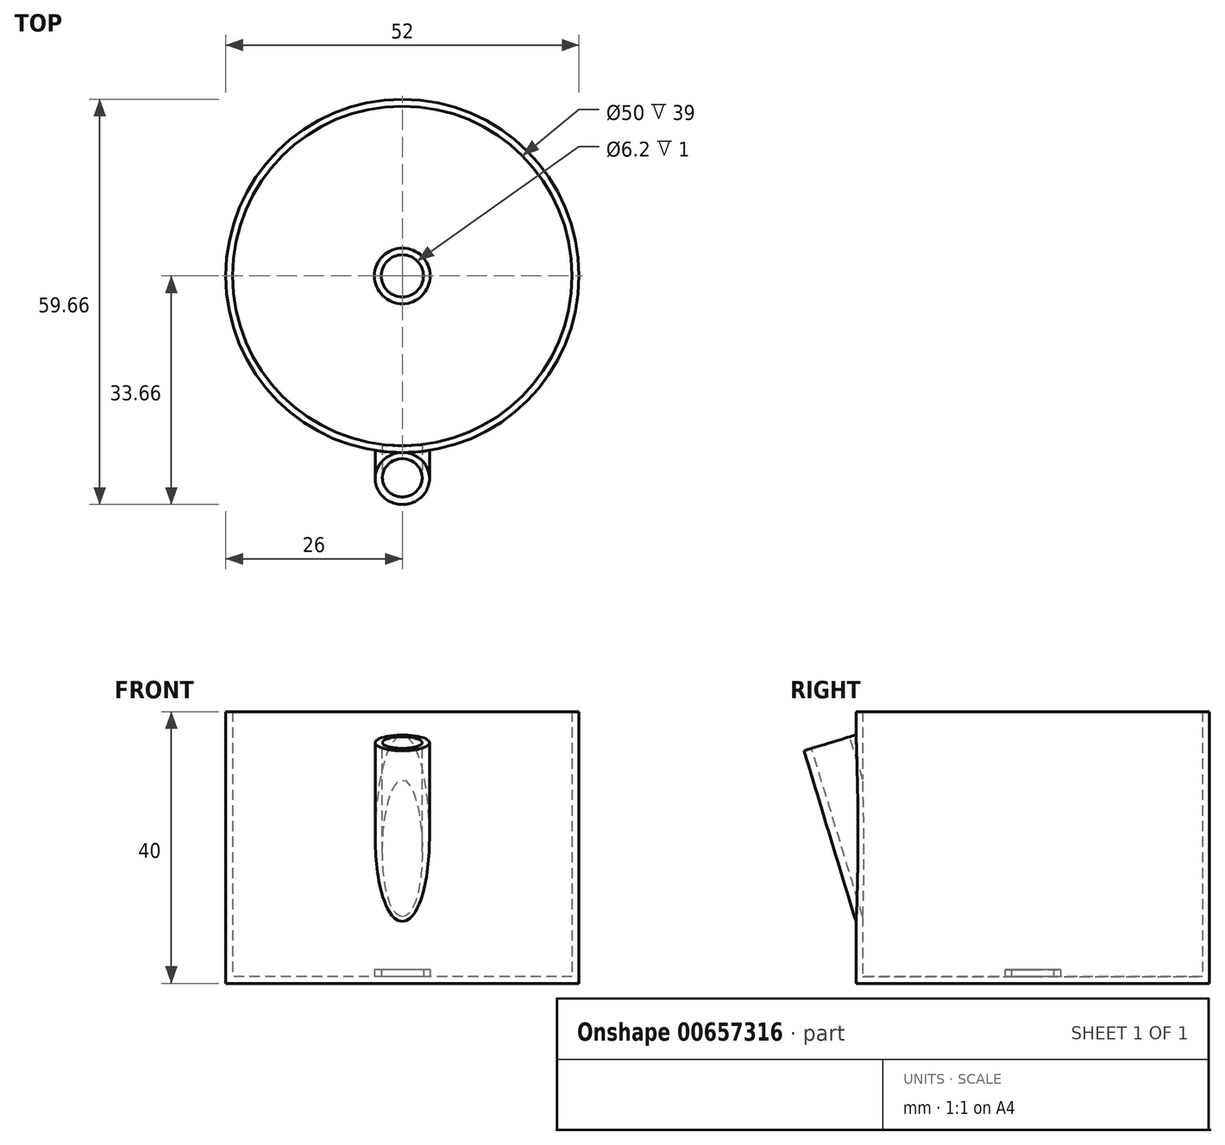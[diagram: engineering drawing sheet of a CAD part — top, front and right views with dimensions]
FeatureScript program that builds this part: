
annotation { "Feature Type Name" : "Feature", "Feature Type Description" : "" }
export const myFeature = defineFeature(function(context is Context, id is Id, definition is map)
    precondition{}
    {
        {
            var Q0;
            Q0=qCreatedBy(makeId("Top.planeOp"),FACE);
            var sketch = newSketch(context, id + "F0", { "sketchPlane" : qUnion([Q0])});
            skCircle(sketch, "E0", {"center": v(0, 0) * mm, "radius": 25 * mm});
            skCircle(sketch, "E1", {"center": v(0, 0) * mm, "radius": 26 * mm});
            skSolve(sketch);
        }
        {
            var Q0;
            Q0=makeQuery(id+"F0.imprint","IMPRINT",FACE,{"disambiguationData":[TD([[makeQuery(id+"F0.imprint","IMPRINT",EDGE,{"derivedFrom":sQuery(id+"F0.wireOp",EDGE,"E0")}),1.0]])]});
            extrude(context, id + "F1", {"entities" : qUnion([Q0]), "depth" : 1 * mm, "offsetDistance" : 25 * mm});
        }
        {
            var Q0;
            Q0=makeQuery(id+"F0.imprint","IMPRINT",FACE,{"disambiguationData":[TD([[makeQuery(id+"F0.imprint","IMPRINT",EDGE,{"derivedFrom":sQuery(id+"F0.wireOp",EDGE,"E0")}),-1.0]])]});
            extrude(context, id + "F2", {"entities" : qUnion([Q0]), "operationType" : NewBodyOperationType.ADD, "depth" : 40 * mm, "offsetDistance" : 25 * mm});
        }
        {
            var Q0;
            Q0=makeQuery(id+"F0.imprint","IMPRINT",FACE,{"disambiguationData":[TD([[makeQuery(id+"F0.imprint","IMPRINT",EDGE,{"derivedFrom":sQuery(id+"F0.wireOp",EDGE,"E0")}),1.0]])]});
            var sketch = newSketch(context, id + "F3", { "sketchPlane" : qUnion([Q0])});
            skCircle(sketch, "E2", {"center": v(0, 0) * mm, "radius": 3.1 * mm});
            skCircle(sketch, "E3", {"center": v(0, 0) * mm, "radius": 4.1 * mm});
            skSolve(sketch);
        }
        {
            var Q0;
            Q0=makeQuery(id+"F3.imprint","IMPRINT",FACE,{"disambiguationData":[TD([[makeQuery(id+"F3.imprint","IMPRINT",EDGE,{"derivedFrom":sQuery(id+"F3.wireOp",EDGE,"E2")}),-1.0]])]});
            extrude(context, id + "F4", {"entities" : qUnion([Q0]), "operationType" : NewBodyOperationType.ADD, "depth" : 2 * mm, "offsetDistance" : 25 * mm});
        }
        {
            var Q0;
            Q0=qCreatedBy(makeId("Top.planeOp"),FACE);
            cPlane(context, id + "F5", {"entities" : qUnion([Q0]), "cplaneType" : CPlaneType.OFFSET, "offset" : 40 * mm, "width" : 150 * mm, "height" : 150 * mm});
        }
        {
            var Q0;
            Q0=qCreatedBy(id+"F5.planeOp",FACE);
            var sketch = newSketch(context, id + "F6", { "sketchPlane" : qUnion([Q0])});
            skLineSegment(sketch, "E4", {"start": v(-12.07, -14.76) * mm, "end": v(12.68, -14.76) * mm});
            skSolve(sketch);
        }
        {
            var Q0;
            Q0=sQuery(id+"F6.wireOp",EDGE,"E4");
            cPlane(context, id + "F7", {"entities" : qUnion([Q0]), "cplaneType" : CPlaneType.LINE_ANGLE, "offset" : 25 * mm, "angle" : 106.93 * degree, "width" : 150 * mm, "height" : 150 * mm});
        }
        {
            var Q0;
            Q0=qCreatedBy(id+"F7.planeOp",FACE);
            var sketch = newSketch(context, id + "F8", { "sketchPlane" : qUnion([Q0])});
            skCircle(sketch, "E5", {"center": v(0, -18.23) * mm, "radius": 4 * mm});
            skSolve(sketch);
        }
        {
            var Q0;
            Q0=makeQuery(id+"F8.imprint","IMPRINT",FACE,{"disambiguationData":[TD([[makeQuery(id+"F8.imprint","IMPRINT",EDGE,{"derivedFrom":sQuery(id+"F8.wireOp",EDGE,"E5")}),1.0]])]});
            extrude(context, id + "F9", {"entities" : qUnion([Q0]), "operationType" : NewBodyOperationType.ADD, "endBound" : BoundingType.UP_TO_NEXT, "oppositeDirection" : true, "depth" : 25 * mm, "offsetDistance" : 25 * mm});
        }
        {
            var Q0;
            Q0=makeQuery(id+"F8.imprint","IMPRINT",FACE,{"disambiguationData":[TD([[makeQuery(id+"F8.imprint","IMPRINT",EDGE,{"derivedFrom":sQuery(id+"F8.wireOp",EDGE,"E5")}),1.0]])]});
            var sketch = newSketch(context, id + "F10", { "sketchPlane" : qUnion([Q0])});
            skCircle(sketch, "E6", {"center": v(0, -18.12) * mm, "radius": 2.93 * mm});
            skSolve(sketch);
        }
        {
            var Q0;
            Q0=makeQuery(id+"F10.imprint","IMPRINT",FACE,{"disambiguationData":[TD([[makeQuery(id+"F10.imprint","IMPRINT",EDGE,{"derivedFrom":sQuery(id+"F10.wireOp",EDGE,"E6")}),1.0]])]});
            extrude(context, id + "F11", {"entities" : qUnion([Q0]), "operationType" : NewBodyOperationType.REMOVE, "oppositeDirection" : true, "depth" : 30 * mm, "offsetDistance" : 25 * mm});
        }
    });
